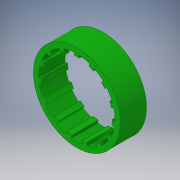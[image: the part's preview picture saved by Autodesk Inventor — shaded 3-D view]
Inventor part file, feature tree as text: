
AUTODESK INVENTOR PART (.ipt)
format: ipt  version: 2018 (Build 220112000, 112)  size: 171,008 bytes
history: native  units: in
note: dims shown in document units (in); Inventor stores cm internally (conversion verified against a paired STEP export)
features: extrude x2, sketch x1, pattern_circular x1
ambient origin geometry x8: Origin, YZ Plane, XZ Plane, XY Plane, X Axis, Y Axis, Z Axis, Center Point
bodies: Solid1 (feature_tree)
feature tree (4):
  sketch  "Sketch1"  dims[d0=1.65in d2=0.05in d3=0.1in d4=0.0275in d5=0.0275in d6=0.5in d7=0.0in d8=0.5in d9=0.0in d10=5.9055in d11=360.0deg]
  extrude  "Extrusion1"  Depth=0.5in
  extrude  "Extrusion2"  Depth=0.5in
  pattern_circular  "Circular Pattern1"  [2 undecoded]
note: 2 required parameter values undecoded (feature->parameter linkage not recoverable at this tier; creation-order binding heuristic only, values carry confidence <= 0.55)
